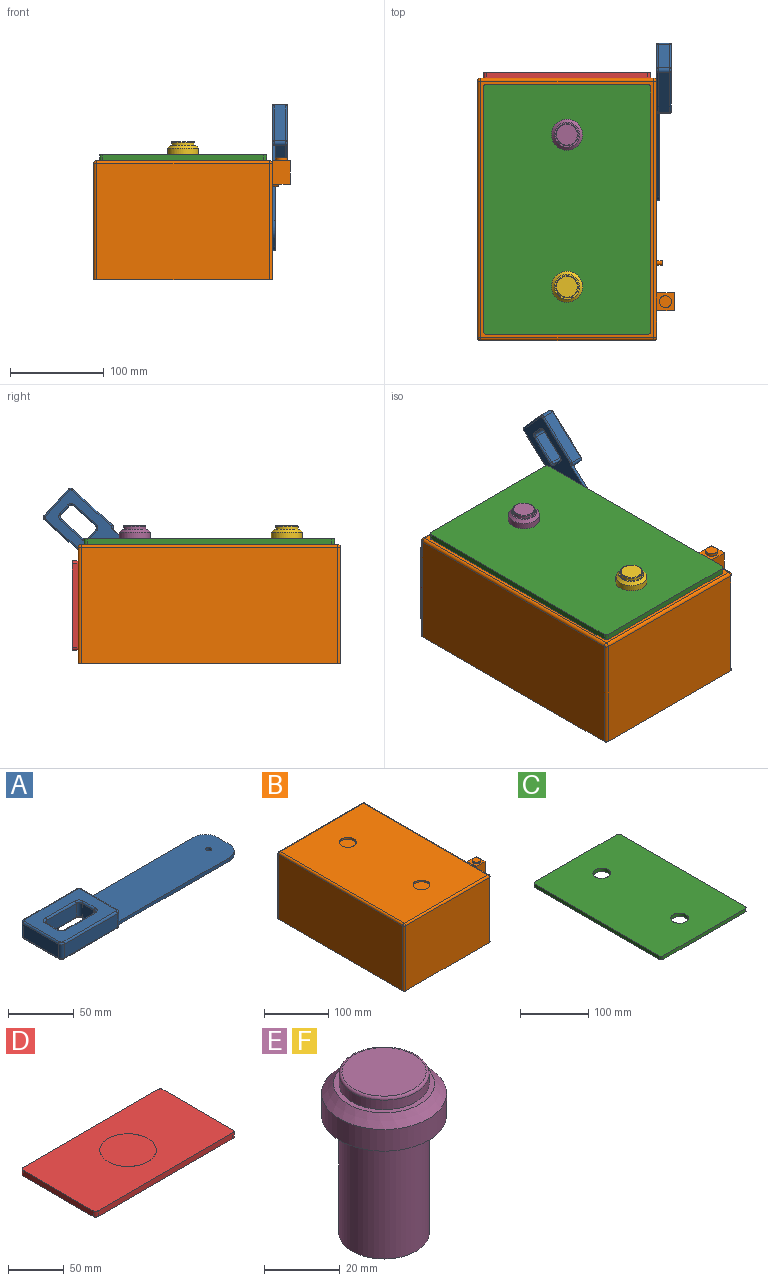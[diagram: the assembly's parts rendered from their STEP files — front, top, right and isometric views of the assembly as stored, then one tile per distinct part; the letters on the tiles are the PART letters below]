
ASSEMBLY  parts=6 mates=5
PART A: 56 faces, bbox 197.1x45x15.9 mm
  f0: cylinder r=1.59mm len=57.15mm, axis (-1,0,0), area 142.5mm2, adj f1,f13,f14,f16
  f1: torus R=1.59mm, axis (0,0,1), area 10.2mm2, adj f0,f2,f13,f17
  f2: cylinder r=1.59mm len=38.1mm, axis (0,-1,0), area 95mm2, adj f1,f3,f13,f18
  f3: torus R=1.59mm, axis (0,0,1), area 10.2mm2, adj f2,f4,f13,f19
  f4: cylinder r=1.59mm len=57.15mm, axis (-1,0,0), area 142.5mm2, adj f3,f13,f15,f20
  f5: cylinder r=1.59mm len=12.7mm, axis (0,-1,0), area 31.7mm2, adj f6,f12,f13,f21
  f6: torus R=4.76mm, axis (0,0,-1), area 14.7mm2, adj f5,f7,f13,f22
  f7: cylinder r=1.59mm len=31.75mm, axis (-1,0,0), area 79.2mm2, adj f6,f8,f13,f23
  f8: torus R=4.76mm, axis (0,0,-1), area 14.7mm2, adj f7,f9,f13,f24
  f9: cylinder r=1.59mm len=12.7mm, axis (0,1,0), area 31.7mm2, adj f8,f10,f13,f25
  f10: torus R=4.76mm, axis (0,0,-1), area 14.7mm2, adj f9,f11,f13,f26
  f11: cylinder r=1.59mm len=31.75mm, axis (1,0,0), area 79.2mm2, adj f10,f12,f13,f27
  f12: torus R=4.76mm, axis (0,0,-1), area 14.7mm2, adj f5,f11,f13,f28
  f13: plane 60.33x41.28mm, normal (0,0,1), area 1589.9mm2, adj f0,f1,f2,f3,f4,f5,f6,f7
  f14: torus R=1.59mm, axis (0,0,1), area 10.2mm2, adj f0,f13,f29,f30
  f15: torus R=1.59mm, axis (0,0,1), area 10.2mm2, adj f4,f13,f29,f31
  f16: plane 57.15x12.7mm, normal (0,1,0), area 725.8mm2, adj f0,f17,f30,f33
  f17: cylinder r=3.17mm len=12.7mm, axis (0,0,1), area 63.3mm2, adj f1,f16,f18,f34
  f18: plane 38.1x12.7mm, normal (-1,0,0), area 483.9mm2, adj f2,f17,f19,f35
  f19: cylinder r=3.17mm len=12.7mm, axis (0,0,-1), area 63.3mm2, adj f3,f18,f20,f36
  f20: plane 57.15x12.7mm, normal (0,-1,0), area 725.8mm2, adj f4,f19,f31,f37
  f21: plane 12.7x12.7mm, normal (-1,0,0), area 161.3mm2, adj f5,f22,f28,f39
  f22: cylinder r=3.17mm len=12.7mm, axis (0,0,-1), area 63.3mm2, adj f6,f21,f23,f40
  f23: plane 31.75x12.7mm, normal (0,1,0), area 403.2mm2, adj f7,f22,f24,f41
  f24: cylinder r=3.17mm len=12.7mm, axis (0,0,-1), area 63.3mm2, adj f8,f23,f25,f42
  f25: plane 12.7x12.7mm, normal (1,0,0), area 161.3mm2, adj f9,f24,f26,f43
  f26: cylinder r=3.17mm len=12.7mm, axis (0,0,-1), area 63.3mm2, adj f10,f25,f27,f44
  f27: plane 31.75x12.7mm, normal (0,-1,0), area 403.2mm2, adj f11,f26,f28,f45
  f28: cylinder r=3.17mm len=12.7mm, axis (0,0,-1), area 63.3mm2, adj f12,f21,f27,f46
  f29: cylinder r=1.59mm len=38.1mm, axis (0,-1,0), area 95mm2, adj f13,f14,f15,f48
  f30: cylinder r=3.17mm len=12.7mm, axis (0,0,1), area 63.3mm2, adj f14,f16,f32,f47,f48
  f31: cylinder r=3.17mm len=12.7mm, axis (0,0,-1), area 63.3mm2, adj f15,f20,f38,f48,f49
  f32: torus R=1.59mm, axis (0,0,1), area 10.2mm2, adj f30,f33,f47,f53
  f33: cylinder r=1.59mm len=57.15mm, axis (-1,0,0), area 142.5mm2, adj f16,f32,f34,f53
  f34: torus R=1.59mm, axis (0,0,1), area 10.2mm2, adj f17,f33,f35,f53
  f35: cylinder r=1.59mm len=38.1mm, axis (0,1,0), area 95mm2, adj f18,f34,f36,f53
  f36: torus R=1.59mm, axis (0,0,1), area 10.2mm2, adj f19,f35,f37,f53
  f37: cylinder r=1.59mm len=57.15mm, axis (-1,0,0), area 142.5mm2, adj f20,f36,f38,f53
  f38: torus R=1.59mm, axis (0,0,1), area 10.2mm2, adj f31,f37,f49,f53
  f39: cylinder r=1.59mm len=12.7mm, axis (0,1,0), area 31.7mm2, adj f21,f40,f46,f53
  f40: torus R=4.76mm, axis (0,0,1), area 14.7mm2, adj f22,f39,f41,f53
  f41: cylinder r=1.59mm len=31.75mm, axis (1,0,0), area 79.2mm2, adj f23,f40,f42,f53
  f42: torus R=4.76mm, axis (0,0,1), area 14.7mm2, adj f24,f41,f43,f53
  f43: cylinder r=1.59mm len=12.7mm, axis (0,-1,0), area 31.7mm2, adj f25,f42,f44,f53
  f44: torus R=4.76mm, axis (0,0,1), area 14.7mm2, adj f26,f43,f45,f53
  f45: cylinder r=1.59mm len=31.75mm, axis (-1,0,0), area 79.2mm2, adj f27,f44,f46,f53
  f46: torus R=4.76mm, axis (0,0,1), area 14.7mm2, adj f28,f39,f45,f53
  f47: plane 122.24x3.18mm, normal (0,1,0), area 383.6mm2, adj f30,f32,f52,f53,f54
  f48: plane 38.1x11.11mm, normal (1,0,0), area 423.4mm2, adj f29,f30,f31,f54
  f49: plane 122.24x3.18mm, normal (0,-1,0), area 383.6mm2, adj f31,f38,f50,f53,f54
  f50: cylinder r=12.7mm len=12.7mm, axis (0,0,1), area 63.3mm2, adj f49,f51,f53,f54
  f51: plane 12.7x3.18mm, normal (1,0,0), area 40.3mm2, adj f50,f52,f53,f54
  f52: cylinder r=12.7mm len=12.7mm, axis (0,0,1), area 63.3mm2, adj f47,f51,f53,f54
  f53: plane 195.26x41.28mm, normal (0,0,-1), area 6645.4mm2, adj f32,f33,f34,f35,f36,f37,f38,f39
  f54: plane 133.35x38.1mm, normal (0,0,1), area 4995mm2, adj f47,f48,f49,f50,f51,f52,f55
  f55: cylinder r=2.29mm len=4.57mm, axis (0,0,-1), area 45.6mm2, adj f53,f54
PART B: 36 faces, bbox 209.6x279.4x130.2 mm
  f0: plane 26.15x26.15mm, normal (0,0,1), area 536.9mm2, adj f5
  f1: plane 26.15x26.15mm, normal (0,0,1), area 536.9mm2, adj f6
  f2: plane 12.7x12.7mm, normal (0,0,1), area 126.7mm2, adj f10
  f3: sphere r=3.17mm, area 15.8mm2, adj f7,f8,f12
  f4: sphere r=3.17mm, area 15.8mm2, adj f8,f9,f14
  f5: cylinder r=13.07mm len=26.15mm, axis (0,0,-1), area 260.8mm2, adj f0,f18
  f6: cylinder r=13.07mm len=26.15mm, axis (0,0,-1), area 260.8mm2, adj f1,f18
  f7: cylinder r=3.17mm len=184.15mm, axis (-1,0,0), area 918.4mm2, adj f3,f16,f17,f18
  f8: cylinder r=3.17mm len=273.05mm, axis (0,-1,0), area 1361.8mm2, adj f3,f4,f13,f18
  f9: cylinder r=3.17mm len=184.15mm, axis (1,0,0), area 918.4mm2, adj f4,f15,f18,f19
  f10: cylinder r=6.35mm len=12.7mm, axis (0,0,1), area 126.7mm2, adj f2,f21
  f11: plane 4.57x4.57mm, normal (1,0,0), area 16.4mm2, adj f24
  f12: cylinder r=3.17mm len=123.83mm, axis (0,0,-1), area 617.5mm2, adj f3,f13,f16,f27
  f13: plane 273.05x123.83mm, normal (-1,0,0), area 33810.4mm2, adj f8,f12,f14,f27
  f14: cylinder r=3.17mm len=123.83mm, axis (0,0,-1), area 617.5mm2, adj f4,f13,f15,f27
  f15: plane 184.15x123.83mm, normal (0,-1,0), area 22802.4mm2, adj f9,f14,f26,f27
  f16: plane 184.15x123.83mm, normal (0,1,0), area 22802.4mm2, adj f7,f12,f27,f28
  f17: sphere r=3.17mm, area 15.8mm2, adj f7,f28,f29
  f18: plane 273.05x184.15mm, normal (0,0,1), area 49208.4mm2, adj f5,f6,f7,f8,f9,f29
  f19: sphere r=3.17mm, area 15.8mm2, adj f9,f26,f29
  f20: plane 19.05x3.18mm, normal (-1,0,0), area 60.5mm2, adj f21,f25,f29,f30
  f21: plane 19.05x19.05mm, normal (0,0,1), area 236.2mm2, adj f10,f20,f22,f25,f30
  f22: plane 25.4x19.05mm, normal (1,0,0), area 483.9mm2, adj f21,f25,f30,f31
  f23: cone r=0.99mm half-angle=59deg, axis (1,0,0), area 14.4mm2, adj f32
  f24: cylinder r=2.29mm len=6.35mm, axis (1,0,0), area 91.2mm2, adj f11,f33
  f25: plane 25.4x19.05mm, normal (0,-1,0), area 483.9mm2, adj f20,f21,f22,f31,f33
  f26: cylinder r=3.17mm len=123.83mm, axis (0,0,-1), area 617.5mm2, adj f15,f19,f27,f33
  f27: plane 279.4x190.5mm, normal (0,0,-1), area 53217mm2, adj f12,f13,f14,f15,f16,f26,f28,f33
  f28: cylinder r=3.17mm len=123.83mm, axis (0,0,-1), area 617.5mm2, adj f16,f17,f27,f33
  f29: cylinder r=3.17mm len=273.05mm, axis (0,1,0), area 1361.8mm2, adj f17,f18,f19,f20,f33
  f30: plane 25.4x19.05mm, normal (0,1,0), area 483.9mm2, adj f20,f21,f22,f31,f33
  f31: plane 19.05x19.05mm, normal (0,0,-1), area 362.9mm2, adj f22,f25,f30,f33
  f32: cylinder r=1.98mm len=25.4mm, axis (-1,0,0), area 316.2mm2, adj f23,f33
  f33: plane 273.05x123.83mm, normal (1,0,0), area 33341.9mm2, adj f24,f25,f26,f27,f28,f29,f30,f31
  f34: plane 4.57x4.57mm, normal (1,0,0), area 16.4mm2, adj f35
  f35: cylinder r=2.29mm len=6.35mm, axis (1,0,0), area 91.2mm2, adj f33,f34
PART C: 12 faces, bbox 177.8x266.7x6.4 mm
  f0: cylinder r=13.07mm len=26.15mm, axis (0,0,1), area 521.6mm2, adj f9,f10
  f1: cylinder r=3.17mm len=6.35mm, axis (0,0,1), area 31.7mm2, adj f2,f8,f9,f10
  f2: plane 260.35x6.35mm, normal (-1,0,0), area 1653.2mm2, adj f1,f3,f9,f10
  f3: cylinder r=3.17mm len=6.35mm, axis (0,0,1), area 31.7mm2, adj f2,f4,f9,f10
  f4: plane 171.45x6.35mm, normal (0,-1,0), area 1088.7mm2, adj f3,f5,f9,f10
  f5: cylinder r=3.17mm len=6.35mm, axis (0,0,1), area 31.7mm2, adj f4,f6,f9,f10
  f6: plane 260.35x6.35mm, normal (1,0,0), area 1653.2mm2, adj f5,f7,f9,f10
  f7: cylinder r=3.17mm len=6.35mm, axis (0,0,1), area 31.7mm2, adj f6,f8,f9,f10
  f8: plane 171.45x6.35mm, normal (0,1,0), area 1088.7mm2, adj f1,f7,f9,f10
  f9: plane 266.7x177.8mm, normal (0,0,1), area 46336.9mm2, adj f0,f1,f2,f3,f4,f5,f6,f7
  f10: plane 266.7x177.8mm, normal (0,0,-1), area 46336.9mm2, adj f0,f1,f2,f3,f4,f5,f6,f7
  f11: cylinder r=13.07mm len=26.15mm, axis (0,0,1), area 521.6mm2, adj f9,f10
PART D: 12 faces, bbox 177.8x95.3x6.4 mm
  f0: plane 177.8x95.25mm, normal (0,0,-1), area 16926.8mm2, adj f1,f2,f3,f4,f5,f6,f7,f8
  f1: cylinder r=3.17mm len=6.35mm, axis (0,0,1), area 31.7mm2, adj f0,f2,f8,f9
  f2: plane 88.9x6.35mm, normal (1,0,0), area 564.5mm2, adj f0,f1,f3,f9
  f3: cylinder r=3.17mm len=6.35mm, axis (0,0,1), area 31.7mm2, adj f0,f2,f4,f9
  f4: plane 171.45x6.35mm, normal (0,1,0), area 1088.7mm2, adj f0,f3,f5,f9
  f5: cylinder r=3.17mm len=6.35mm, axis (0,0,1), area 31.7mm2, adj f0,f4,f6,f9
  f6: plane 88.9x6.35mm, normal (-1,0,0), area 564.5mm2, adj f0,f5,f7,f9
  f7: cylinder r=3.17mm len=6.35mm, axis (0,0,1), area 31.7mm2, adj f0,f6,f8,f9
  f8: plane 171.45x6.35mm, normal (0,-1,0), area 1088.7mm2, adj f0,f1,f7,f9
  f9: plane 177.8x95.25mm, normal (0,0,1), area 14900mm2, adj f1,f2,f3,f4,f5,f6,f7,f8
  f10: plane 50.8x50.8mm, normal (0,0,1), area 2026.8mm2, adj f11
  f11: cylinder r=25.4mm len=50.8mm, axis (0,0,1), area 2mm2, adj f9,f10
PART E: 9 faces, bbox 33x33x52.1 mm
  f0: torus R=11.11mm, axis (0,0,-1), area 87.2mm2, adj f1,f2
  f1: cylinder r=11.87mm len=23.75mm, axis (0,0,-1), area 227.4mm2, adj f0,f4
  f2: plane 22.23x22.23mm, normal (0,0,1), area 387.9mm2, adj f0
  f3: cone r=14.92mm half-angle=45deg, axis (0,0,-1), area 421mm2, adj f4,f5
  f4: plane 26.67x26.67mm, normal (0,0,1), area 115.7mm2, adj f1,f3
  f5: cylinder r=16.51mm len=33.02mm, axis (0,0,-1), area 724.6mm2, adj f3,f8
  f6: cylinder r=11.94mm len=38.1mm, axis (0,0,-1), area 2857.8mm2, adj f7,f8
  f7: plane 23.88x23.88mm, normal (0,0,-1), area 447.7mm2, adj f6
  f8: plane 33.02x33.02mm, normal (0,0,-1), area 408.6mm2, adj f5,f6
PART F: same geometry as E
PLACE A rot(axis=(-0.38,0.85,-0.38),99.5deg) t=(201.41,148.83,-70.73)mm
PLACE B t=(10.91,5.1,1.93)mm fixed
PLACE C rot(axis=(0,-1,0),180deg) t=(106.16,144.8,8.28)mm
PLACE D rot(axis=(-1,0,0),90deg) t=(10.91,284.5,-133)mm
PLACE E t=(106.16,224.17,22.25)mm
PLACE F t=(106.16,62.25,22.25)mm
MATE fastened B.f16 <-> D.f11  axis (0,1,0) through (106.16,284.5,-63.15)mm
MATE fastened C.f11 <-> E.f0  axis (0,0,1) through (106.16,224.17,8.28)mm
MATE fastened C.f0 <-> B.f6  axis (0,0,-1) through (106.16,62.25,1.93)mm
MATE fastened F.f0 <-> C.f0  axis (0,0,-1) through (106.16,62.25,8.28)mm
MATE revolute B.f23 <-> A.f55  axis (1,0,0) through (201.41,173.37,-74.27)mm
